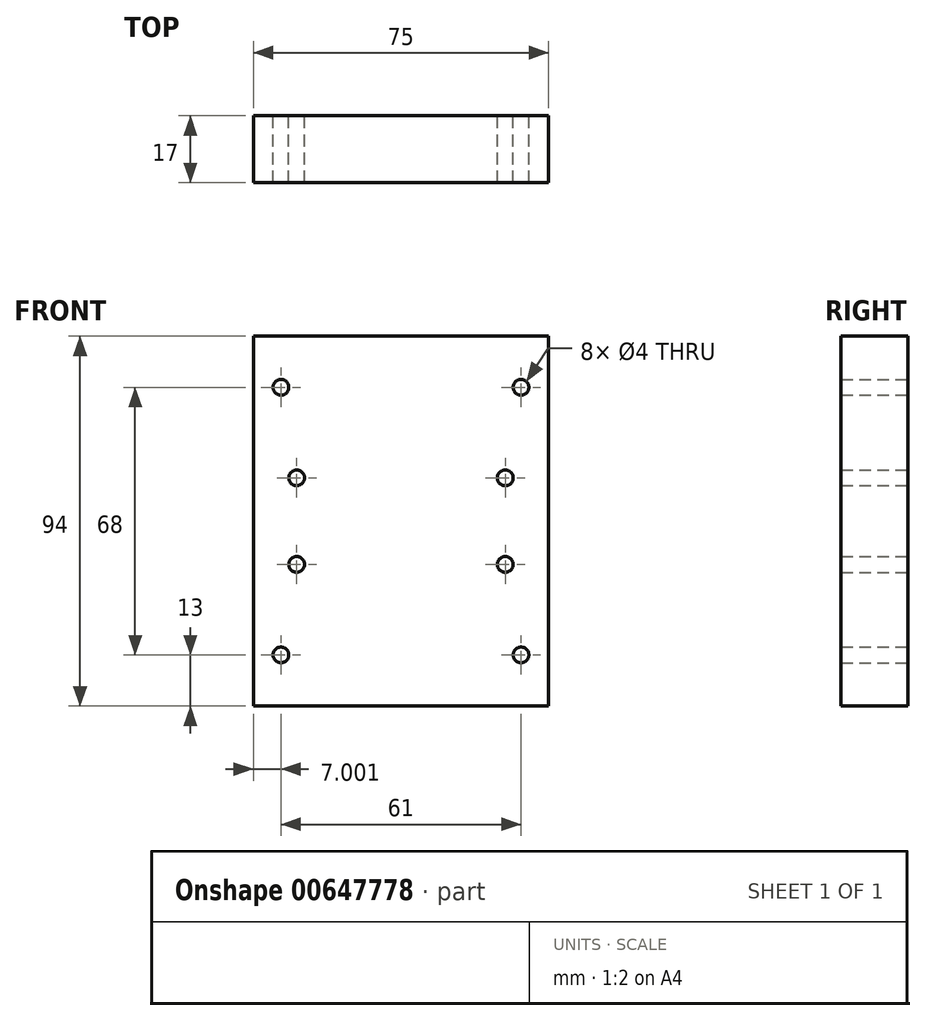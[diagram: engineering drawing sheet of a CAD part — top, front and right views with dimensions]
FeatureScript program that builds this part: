
annotation { "Feature Type Name" : "Feature", "Feature Type Description" : "" }
export const myFeature = defineFeature(function(context is Context, id is Id, definition is map)
    precondition{}
    {
        {
            var Q0;
            Q0=qCreatedBy(makeId("Front.planeOp"),FACE);
            var sketch = newSketch(context, id + "F0", { "sketchPlane" : qUnion([Q0])});
            skLineSegment(sketch, "E0.bottom", {"start": v(-38.98, 47) * mm, "end": v(36.02, 47) * mm});
            skLineSegment(sketch, "E0.top", {"start": v(-38.98, -47) * mm, "end": v(36.02, -47) * mm});
            skLineSegment(sketch, "E0.left", {"start": v(-38.98, 47) * mm, "end": v(-38.98, -47) * mm});
            skLineSegment(sketch, "E0.right", {"start": v(36.02, 47) * mm, "end": v(36.02, -47) * mm});
            skCircle(sketch, "E1", {"center": v(-31.98, 34) * mm, "radius": 2 * mm});
            skCircle(sketch, "E2", {"center": v(-27.98, 11) * mm, "radius": 2 * mm});
            skCircle(sketch, "E3", {"center": v(25.02, 11) * mm, "radius": 2 * mm});
            skCircle(sketch, "E4", {"center": v(29.02, 34) * mm, "radius": 2 * mm});
            skCircle(sketch, "E5.MirrorC", {"center": v(-31.98, -34) * mm, "radius": 2 * mm});
            skCircle(sketch, "E6.MirrorC", {"center": v(-27.98, -11) * mm, "radius": 2 * mm});
            skCircle(sketch, "E7.MirrorC", {"center": v(29.02, -34) * mm, "radius": 2 * mm});
            skCircle(sketch, "E8.MirrorC", {"center": v(25.02, -11) * mm, "radius": 2 * mm});
            skSolve(sketch);
        }
        {
            var Q0;
            Q0=makeQuery(id+"F0.imprint","IMPRINT",FACE,{"disambiguationData":[TD([[makeQuery(id+"F0.imprint","IMPRINT",EDGE,{"derivedFrom":sQuery(id+"F0.wireOp",EDGE,"E0.bottom")}),-1.0]])]});
            extrude(context, id + "F1", {"entities" : qUnion([Q0]), "depth" : 17 * mm, "offsetDistance" : 25 * mm});
        }
    });
